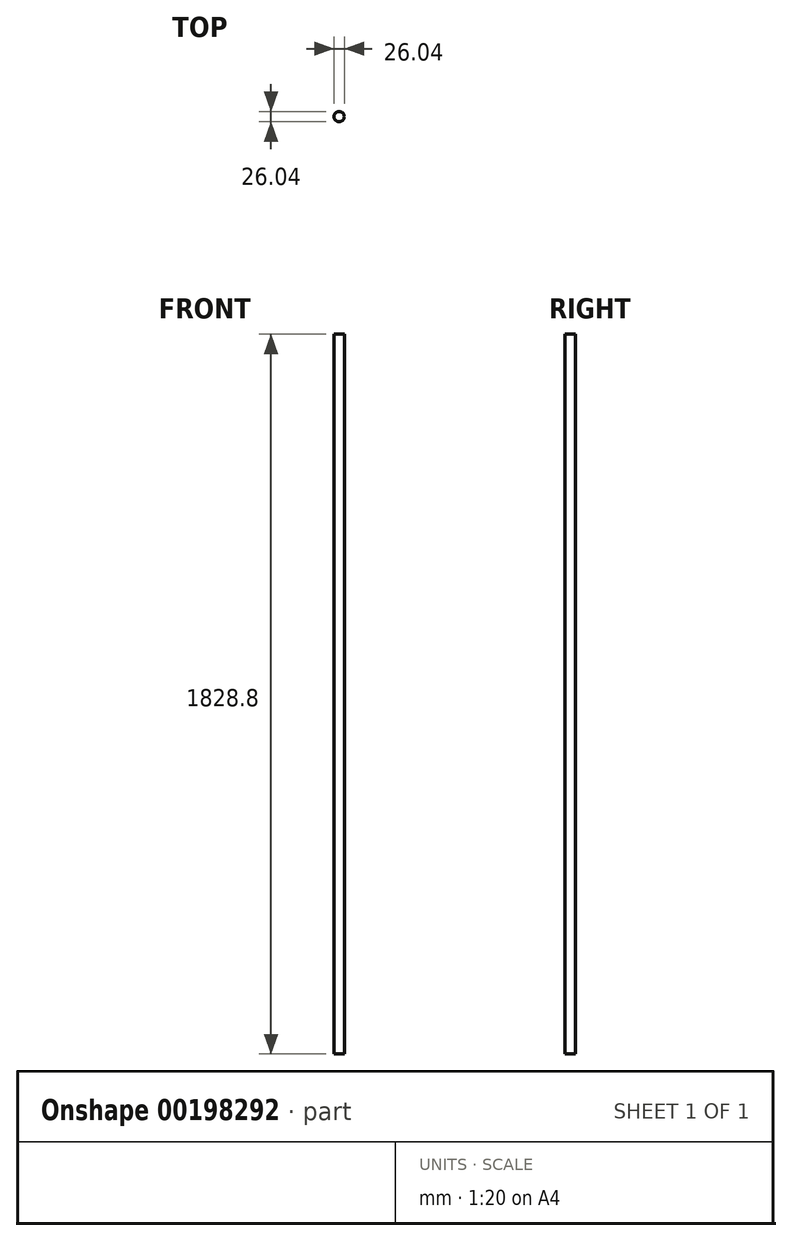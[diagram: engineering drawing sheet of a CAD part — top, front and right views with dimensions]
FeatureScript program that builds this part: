
annotation { "Feature Type Name" : "Feature", "Feature Type Description" : "" }
export const myFeature = defineFeature(function(context is Context, id is Id, definition is map)
    precondition{}
    {
        {
            var Q0;
            Q0=qCreatedBy(makeId("Top.planeOp"),FACE);
            var sketch = newSketch(context, id + "F0", { "sketchPlane" : qUnion([Q0])});
            skCircle(sketch, "E0", {"center": v(0, 0) * mm, "radius": 13.02 * mm});
            skSolve(sketch);
        }
        {
            var Q0;
            Q0=makeQuery(id+"F0.imprint","IMPRINT",FACE,{"disambiguationData":[TD([[makeQuery(id+"F0.imprint","IMPRINT",EDGE,{"derivedFrom":sQuery(id+"F0.wireOp",EDGE,"E0")}),1.0]])]});
            extrude(context, id + "F1", {"entities" : qUnion([Q0]), "depth" : 914.4 * mm, "hasSecondDirection" : true, "secondDirectionOppositeDirection" : true, "secondDirectionDepth" : 914.4 * mm});
        }
    });
